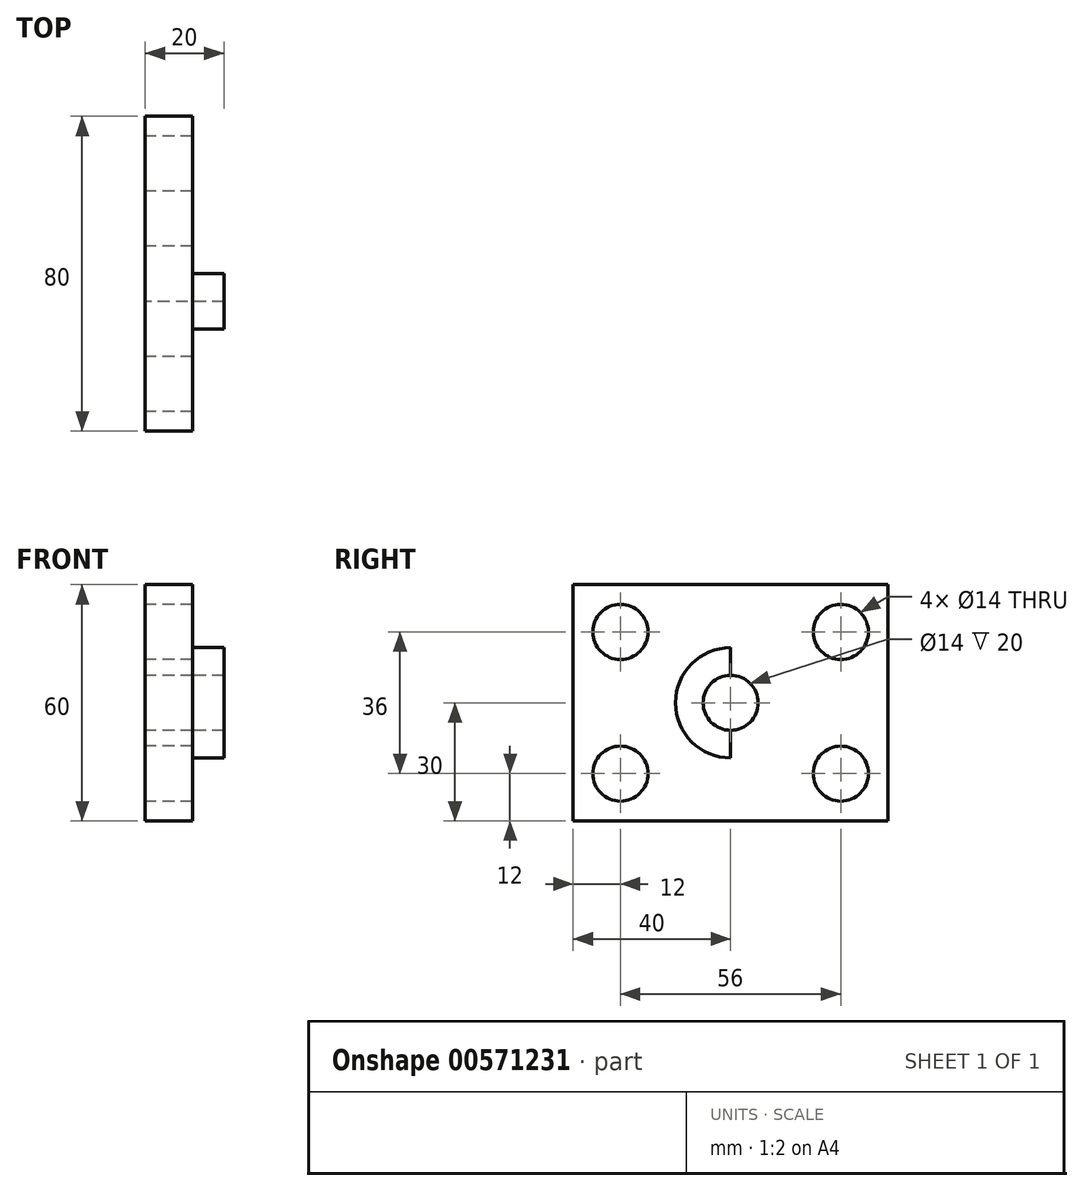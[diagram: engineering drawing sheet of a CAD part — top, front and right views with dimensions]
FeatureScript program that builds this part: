
annotation { "Feature Type Name" : "Feature", "Feature Type Description" : "" }
export const myFeature = defineFeature(function(context is Context, id is Id, definition is map)
    precondition{}
    {
        {
            var Q0;
            Q0=qCreatedBy(makeId("Right.planeOp"),FACE);
            var sketch = newSketch(context, id + "F0", { "sketchPlane" : qUnion([Q0])});
            skLineSegment(sketch, "E0.bottom", {"start": v(0, 0) * mm, "end": v(-80, 0) * mm});
            skLineSegment(sketch, "E0.top", {"start": v(0, 60) * mm, "end": v(-80, 60) * mm});
            skLineSegment(sketch, "E0.left", {"start": v(0, 0) * mm, "end": v(0, 60) * mm});
            skLineSegment(sketch, "E0.right", {"start": v(-80, 0) * mm, "end": v(-80, 60) * mm});
            skCircle(sketch, "E1", {"center": v(-68, 48) * mm, "radius": 7 * mm});
            skLineSegment(sketch, "E2", {"start": v(-40, 60) * mm, "end": v(-40, 0) * mm, "construction": true});
            skLineSegment(sketch, "E3", {"start": v(-80, 30) * mm, "end": v(0, 30) * mm, "construction": true});
            skCircle(sketch, "E4", {"center": v(-12, 48) * mm, "radius": 7 * mm});
            skCircle(sketch, "E5", {"center": v(-12, 12) * mm, "radius": 7 * mm});
            skCircle(sketch, "E6", {"center": v(-68, 12) * mm, "radius": 7 * mm});
            skCircle(sketch, "E7", {"center": v(-40, 30) * mm, "radius": 7 * mm});
            skLineSegment(sketch, "E8", {"start": v(-40, 44) * mm, "end": v(-40, 37) * mm});
            skLineSegment(sketch, "E9", {"start": v(-40, 16) * mm, "end": v(-40, 23) * mm});
            skArc(sketch, "E10", {"start": v(-40, 44) * mm, "mid": v(-54, 30) * mm, "end": v(-40, 16) * mm});
            skSolve(sketch);
        }
        {
            var Q0;
            Q0=makeQuery(id+"F0.imprint","IMPRINT",FACE,{"disambiguationData":[TD([[makeQuery(id+"F0.imprint","IMPRINT",EDGE,{"derivedFrom":sQuery(id+"F0.wireOp",EDGE,"E0.bottom")}),-1.0]])]});
            extrude(context, id + "F1", {"entities" : qUnion([Q0]), "depth" : 12 * mm, "offsetDistance" : 25 * mm});
        }
        {
            var Q0;
            {var subQ0=sQuery(id+"F0.wireOp",EDGE,"E8");Q0=makeQuery(id+"F0.imprint","IMPRINT",FACE,{"disambiguationData":[TD([[makeQuery(id+"F0.imprint","IMPRINT",EDGE,{"derivedFrom":subQ0}),-1.0]])]});}
            extrude(context, id + "F2", {"entities" : qUnion([Q0]), "operationType" : NewBodyOperationType.ADD, "depth" : 20 * mm, "offsetDistance" : 25 * mm});
        }
    });
